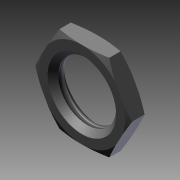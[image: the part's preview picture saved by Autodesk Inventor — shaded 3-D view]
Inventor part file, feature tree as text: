
AUTODESK INVENTOR PART (.ipt)
format: ipt  version: 2015 (Build 190159000, 159)  size: 135,680 bytes
history: native  units: in
note: dims shown in document units (in); Inventor stores cm internally (conversion verified against a paired STEP export)
features: other x7, sketch x3, revolve x2, extrude x1, thread x1
ambient origin geometry x8: Origin, YZ Plane, XZ Plane, XY Plane, X Axis, Y Axis, Z Axis, Center Point
bodies: Solid1 (feature_tree)
feature tree (14):
  revolve  "Revolution1"  [1 undecoded]
  extrude  "Extrusion1"  Depth=0.0203in TaperAngle=0.0deg
  revolve  "Revolution2"  [1 undecoded]
  thread  "Thread1"  [1 undecoded]
  other  "nut_XY"
  other  "nut_YZ"
  other  "nut_ZX"
  other  "nut_X"
  other  "nut_Y"
  other  "nut_Z"
  other  "nut_Center"
  sketch  "Sketch_1"  dims[d0=360.0deg d1=0.118in d2=0.0in]
  sketch  "Sketch_2"  dims[d3=360.0deg d4=0.0203in d5=0.0in]
  sketch  "Sketch_6"
note: 3 required parameter values undecoded (feature->parameter linkage not recoverable at this tier; creation-order binding heuristic only, values carry confidence <= 0.55)